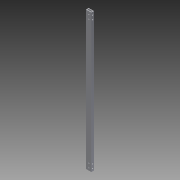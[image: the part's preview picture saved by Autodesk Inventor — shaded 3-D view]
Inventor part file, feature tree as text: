
AUTODESK INVENTOR PART (.ipt)
format: ipt  version: 2013 (Build 170138000, 138)  size: 327,680 bytes
history: native  units: in
note: dims shown in document units (in); Inventor stores cm internally (conversion verified against a paired STEP export)
features: extrude x3, sketch x3, plane x1, reference x1
ambient origin geometry x8: Origin, YZ Plane, XZ Plane, XY Plane, X Axis, Y Axis, Z Axis, Center Point
bodies: Solid1 (feature_tree)
feature tree (8):
  extrude  "Extrusion1"  Depth=0.125in
  extrude  "Extrusion2"  Depth=0.5in
  plane  "Work Plane1"
  extrude  "Extrusion3"  Depth=0.25in
  sketch  "Sketch1"  dims[d0=1.0in d2=0.125in]
  sketch  "Sketch2"  dims[d3=26.0in d4=0.0in d5=0.5in]
  reference  "Reference1"
  sketch  "Sketch3"  dims[d6=1.0in d7=0.0in d8=0.25in d10=0.5in d11=0.75in d12=0.5in d13=0.75in d14=1.0in d15=0.0in]
